# Revit family: КОМ1-ВО
name_source: partatom
category: Арматура воздуховодов
units: mm (PartAtom-declared; Revit-internal decimal feet)

## family parameters
Всегда вертикально = Да
На основе рабочей плоскости = Нет
Общий = Нет
При загрузке вырезать с полостями = Нет
Размер круглого соединителя = Использовать диаметр
Тип детали = Присоединяется

## types (11) — shared parameters
00_20_Виробник = Вентс
00_20_Назва = Зворотній клапан
URL = https://vents.ua
Изготовитель = Вентс
Класифікація навантаження = HVAC
Матеріал зони обслуговуваня = <По категории>
Матеріал корпусу = Метал, пофарбований, синій, матовий RAL 5007
zero-valued in all types: Отметка по умолчанию

## per-type parameters (varying)
| type | D1 | D2 | Dn | Dy | L | R1 | d | l | n | t | Вага | Довжина | Діаметр |
| КОМ1-ВО-400 | 450 мм | 490 мм | 410 мм | 400 мм | 500 мм | 225 мм | 8 мм | 250 мм | 12 | 495 мм | 8.10 кг | 500 мм | 490 мм |
| КОМ1-ВО-450 | 500 мм | 540 мм | 460 мм | 450 мм | 550 мм | 250 мм | 8 мм | 275 мм | 12 | 545 мм | 9.80 кг | 550 мм | 540 мм |
| КОМ1-ВО-500 | 560 мм | 600 мм | 510 мм | 500 мм | 600 мм | 280 мм | 12 мм | 300 мм | 12 | 595 мм | 14.40 кг | 600 мм | 600 мм |
| КОМ1-ВО-560 | 620 мм | 660 мм | 570 мм | 560 мм | 660 мм | 310 мм | 12 мм | 330 мм | 12 | 655 мм | 17.50 кг | 660 мм | 660 мм |
| КОМ1-ВО-630 | 690 мм | 730 мм | 640 мм | 630 мм | 730 мм | 345 мм | 12 мм | 365 мм | 12 | 725 мм | 21.40 кг | 730 мм | 730 мм |
| КОМ1-ВО-710 | 770 мм | 810 мм | 720 мм | 710 мм | 810 мм | 385 мм | 12 мм | 405 мм | 16 | 805 мм | 26.80 кг | 810 мм | 810 мм |
| КОМ1-ВО-800 | 860 мм | 900 мм | 810 мм | 800 мм | 900 мм | 430 мм | 12 мм | 450 мм | 16 | 895 мм | 33.20 кг | 900 мм | 900 мм |
| КОМ1-ВО-900 | 970 мм | 1015 мм | 910 мм | 900 мм | 1000 мм | 485 мм | 15 мм | 500 мм | 16 | 995 мм | 53.70 кг | 1000 мм | 1015 мм |
| КОМ1-ВО-1000 | 1070 мм | 1115 мм | 1010 мм | 1000 мм | 1100 мм | 535 мм | 15 мм | 550 мм | 16 | 1095 мм | 65.00 кг | 1100 мм | 1115 мм |
| КОМ1-ВО-1120 | 1190 мм | 1270 мм | 1130 мм | 1120 мм | 1220 мм | 595 мм | 15 мм | 610 мм | 20 | 1215 мм | 82.10 кг | 1220 мм | 1270 мм |
| КОМ1-ВО-1250 | 1320 мм | 1400 мм | 1260 мм | 1250 мм | 1350 мм | 660 мм | 15 мм | 675 мм | 20 | 1345 мм | 100.30 кг | 1350 мм | 1400 мм |

note: column(s) folded — value = type name in every type: 00_20_Тип
